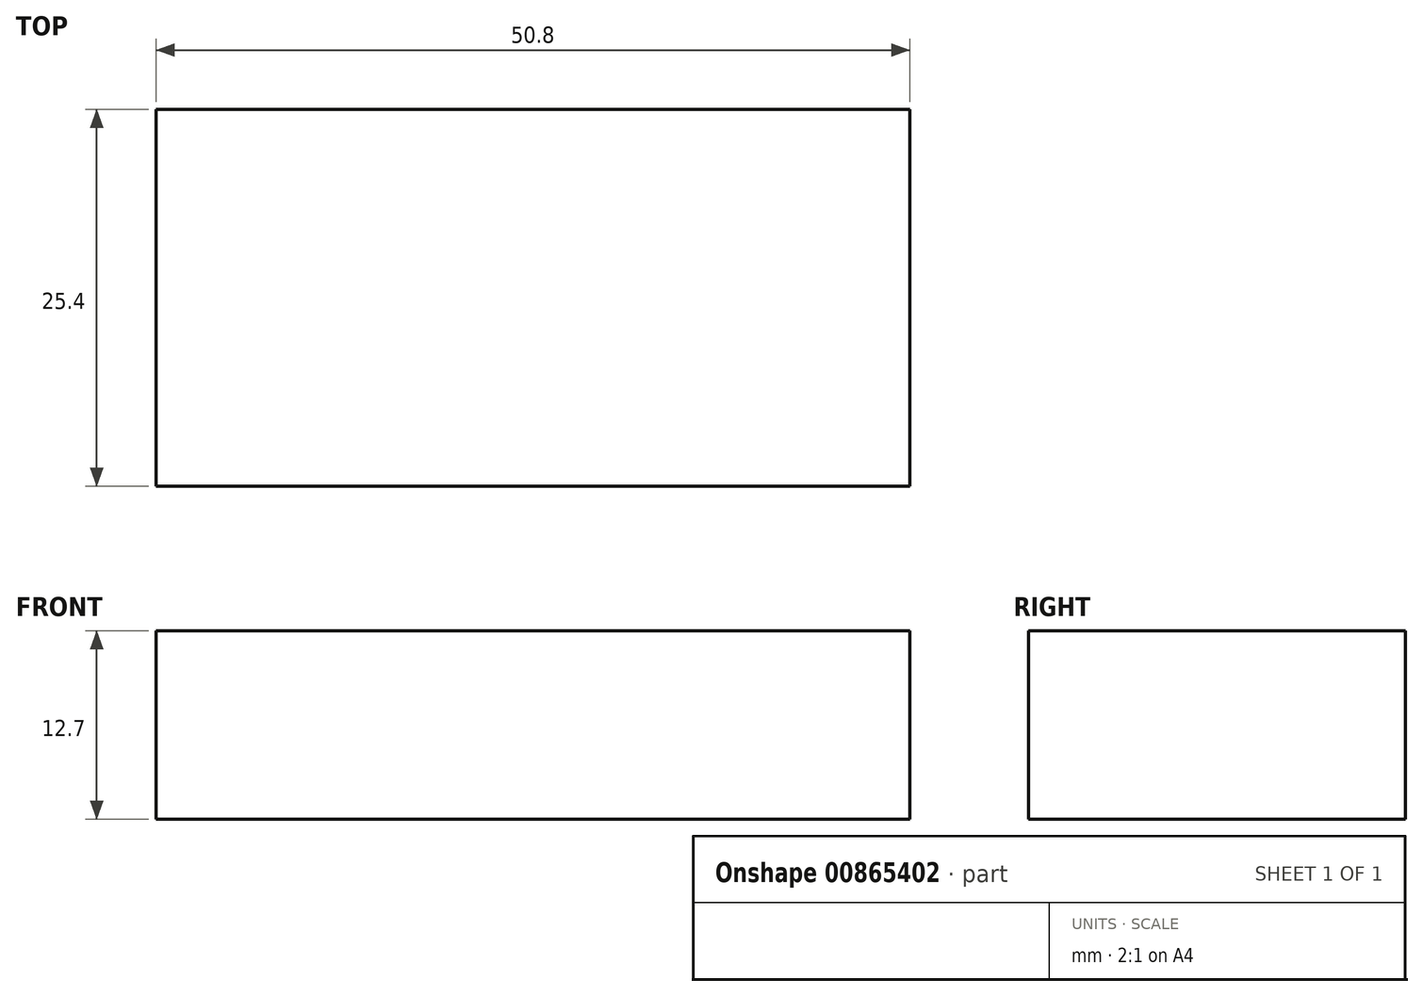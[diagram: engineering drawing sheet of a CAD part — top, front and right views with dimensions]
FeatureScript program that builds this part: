
annotation { "Feature Type Name" : "Feature", "Feature Type Description" : "" }
export const myFeature = defineFeature(function(context is Context, id is Id, definition is map)
    precondition{}
    {
        {
            var Q0;
            Q0=qCreatedBy(makeId("Top.planeOp"),FACE);
            var sketch = newSketch(context, id + "F0", { "sketchPlane" : qUnion([Q0])});
            skLineSegment(sketch, "E0.bottom", {"start": v(0, 0) * mm, "end": v(50.8, 0) * mm});
            skLineSegment(sketch, "E0.top", {"start": v(0, 25.4) * mm, "end": v(50.8, 25.4) * mm});
            skLineSegment(sketch, "E0.left", {"start": v(0, 0) * mm, "end": v(0, 25.4) * mm});
            skLineSegment(sketch, "E0.right", {"start": v(50.8, 0) * mm, "end": v(50.8, 25.4) * mm});
            skSolve(sketch);
        }
        {
            var Q0;
            Q0 = qSketchRegion(id + "F0", true);
            extrude(context, id + "F1", {"entities" : qUnion([Q0]), "depth" : 12.7 * mm, "offsetDistance" : 25.4 * mm});
        }
    });
